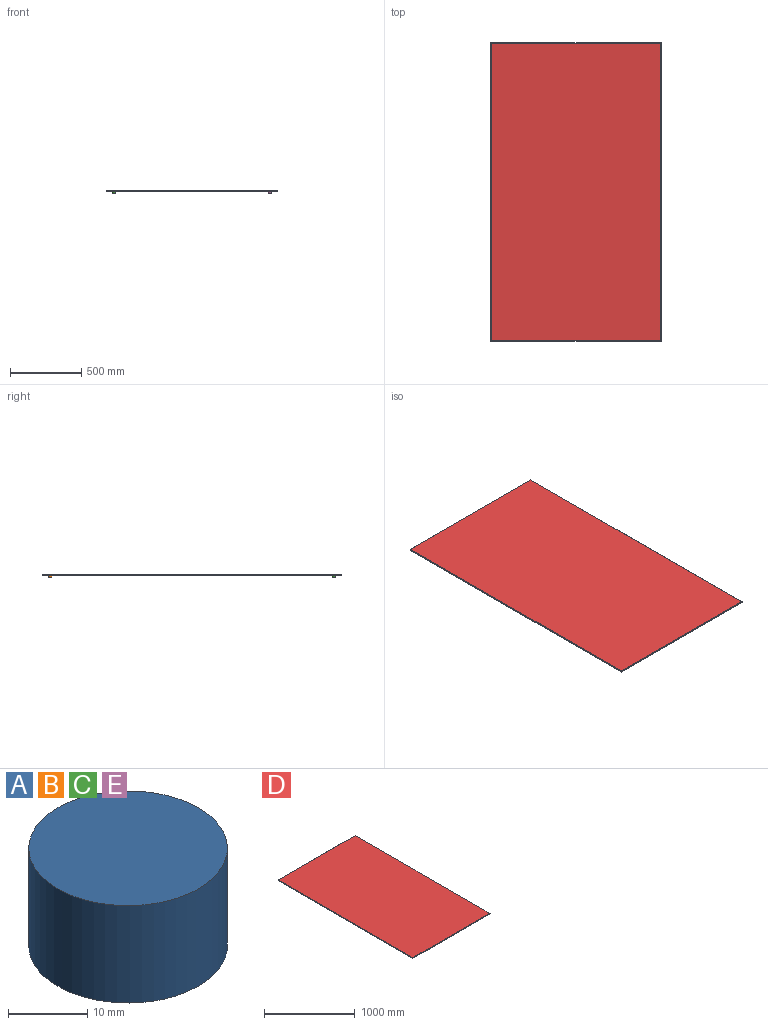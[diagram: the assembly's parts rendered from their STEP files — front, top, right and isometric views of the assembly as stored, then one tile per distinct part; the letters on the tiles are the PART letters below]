
ASSEMBLY  parts=5 mates=4
PART A: 3 faces, bbox 25x25x15 mm
  f0: cylinder r=12.5mm len=25mm, axis (0,0,-1), area 1178.1mm2, adj f1,f2
  f1: plane 25x25mm, normal (0,0,1), area 490.9mm2, adj f0
  f2: plane 25x25mm, normal (0,0,-1), area 490.9mm2, adj f0
PART B: same geometry as A
PART C: same geometry as A
PART D: 14 faces, bbox 1200x2100x10 mm
  f0: plane 2100x4mm, normal (1,0,0), area 8400mm2, adj f1,f3,f7,f11
  f1: plane 1200x4mm, normal (0,1,0), area 4800mm2, adj f0,f2,f9,f13
  f2: plane 2100x4mm, normal (-1,0,0), area 8400mm2, adj f1,f3,f8,f12
  f3: plane 1200x4mm, normal (0,-1,0), area 4800mm2, adj f0,f2,f6,f10
  f4: plane 2094x1194mm, normal (0,0,1), area 2500236mm2, adj f10,f11,f12,f13
  f5: plane 2094x1194mm, normal (0,0,-1), area 2500236mm2, adj f6,f7,f8,f9
  f6: plane 1200x3mm, normal (0,-0.71,-0.71), area 5078.4mm2, adj f3,f5,f7,f8
  f7: plane 2100x3mm, normal (0.71,0,-0.71), area 8896.8mm2, adj f0,f5,f6,f9
  f8: plane 2100x3mm, normal (-0.71,0,-0.71), area 8896.8mm2, adj f2,f5,f6,f9
  f9: plane 1200x3mm, normal (0,0.71,-0.71), area 5078.4mm2, adj f1,f5,f7,f8
  f10: plane 1200x3mm, normal (0,-0.71,0.71), area 5078.4mm2, adj f3,f4,f11,f12
  f11: plane 2100x3mm, normal (0.71,0,0.71), area 8896.8mm2, adj f0,f4,f10,f13
  f12: plane 2100x3mm, normal (-0.71,0,0.71), area 8896.8mm2, adj f2,f4,f10,f13
  f13: plane 1200x3mm, normal (0,0.71,0.71), area 5078.4mm2, adj f1,f4,f11,f12
PART E: same geometry as A
PLACE A rot(axis=(1,0,0),180deg) t=(547,997,0)mm
PLACE B t=(-547,997,-15)mm
PLACE C t=(-547,-997,-15)mm
PLACE D at identity fixed
PLACE E t=(547,-997,-15)mm
MATE fastened A.f0 <-> D.f5  axis (0,0,1) through (547,997,0)mm
MATE fastened C.f0 <-> D.f5  axis (0,0,1) through (-547,-997,0)mm
MATE fastened B.f0 <-> D.f5  axis (0,0,-1) through (-547,997,0)mm
MATE fastened E.f0 <-> D.f5  axis (0,0,-1) through (547,-997,0)mm
